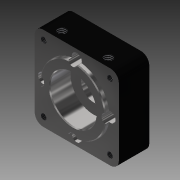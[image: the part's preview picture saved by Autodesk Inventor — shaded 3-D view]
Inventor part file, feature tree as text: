
AUTODESK INVENTOR PART (.ipt)
format: ipt  version: 2013 (Build 170138000, 138)  size: 235,520 bytes
history: native  units: in
note: dims shown in document units (in); Inventor stores cm internally (conversion verified against a paired STEP export)
features: thread x8, extrude x5, sketch x3, fillet x1, chamfer x1
ambient origin geometry x8: Origin, YZ Plane, XZ Plane, XY Plane, X Axis, Y Axis, Z Axis, Center Point
bodies: Solid1 (feature_tree)
feature tree (18):
  sketch  "Sketch1"  dims[d0=0.75in d2=2.5in]
  extrude  "Extrusion1"  Depth=2.5in
  extrude  "Extrusion2"  Depth=0.185in
  extrude  "Extrusion3"  Depth=1.0in
  fillet  "Fillet1"  Radius=1.0in
  chamfer  "Chamfer1"  Distance=1.0in
  thread  "Thread1"  [1 undecoded]
  thread  "Thread2"  [1 undecoded]
  thread  "Thread3"  [1 undecoded]
  thread  "Thread4"  [1 undecoded]
  extrude  "Extrusion4"  Depth=0.1575in
  extrude  "Extrusion5"  Depth=0.97in
  thread  "Thread5"  [1 undecoded]
  thread  "Thread6"  [1 undecoded]
  thread  "Thread7"  [1 undecoded]
  thread  "Thread8"  [1 undecoded]
  sketch  "Sketch2"  dims[d3=2.5in d4=0.185in]
  sketch  "Sketch3"  dims[d5=1.94in d6=1.0in d7=1.0in d8=1.0in d9=1.0in d10=1.375in d11=0.902in d12=0.0in d13=2.126in d14=2.126in d15=0.1575in d16=0.97in d17=0.3in d18=0.5in d19=0.0in d20=0.1181in d21=0.0in d22=0.25in d23=0.025in d24=0.125in d25=45.0deg d26=0.167in d27=1.0in d28=0.0in d29=1.0in d30=0.0in d31=1.0in d32=0.0in d33=1.0in d34=0.0in d35=1.378in d37=0.25in d38=0.652in d39=0.5in d40=0.0in d41=0.25in d43=0.652in d44=1.378in d45=0.5in d46=0.0in d47=1.0in d48=0.0in d49=1.0in d50=0.0in d51=1.0in d52=0.0in d53=1.0in d54=0.0in]
note: 8 required parameter values undecoded (feature->parameter linkage not recoverable at this tier; creation-order binding heuristic only, values carry confidence <= 0.55)
